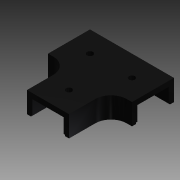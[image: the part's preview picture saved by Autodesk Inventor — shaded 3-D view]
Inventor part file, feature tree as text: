
AUTODESK INVENTOR PART (.ipt)
format: ipt  version: 2014 (Build 180170000, 170)  size: 173,056 bytes
history: native  units: in
note: dims shown in document units (in); Inventor stores cm internally (conversion verified against a paired STEP export)
features: extrude x6, sketch x6, other x3, split x1, fillet x1
ambient origin geometry x8: Origin, YZ Plane, XZ Plane, XY Plane, X Axis, Y Axis, Z Axis, Center Point
bodies: Solid1 (feature_tree)
feature tree (17):
  extrude  "Extrusion1"  Depth=1.0in
  extrude  "Extrusion2"  Depth=0.5in TaperAngle=0.0deg
  extrude  "Extrusion3"  Depth=0.75in
  extrude  "Extrusion4"  Depth=1.75in TaperAngle=0.0deg
  extrude  "Extrusion5"  Depth=0.75in
  split  "Split1"
  other  "Lip1"
  other  "Lip2"
  other  "Lip3"
  extrude  "Extrusion6"  Depth=0.375in
  fillet  "Fillet1"  Radius=1.0in
  sketch  "Sketch1"  dims[d0=1.0in d1=1.0in]
  sketch  "Sketch2"  dims[d2=2.0in d3=0.0in d4=0.5in d5=0.0in]
  sketch  "Sketch4"  dims[d6=0.5in d7=0.0in d8=0.75in]
  sketch  "Sketch5"  dims[d9=0.75in d10=1.75in d11=0.0in]
  sketch  "Sketch6"  dims[d12=0.75in d13=0.75in]
  sketch  "Sketch7"  dims[d14=1.75in d15=0.0in d16=0.03in d17=0.03in d18=0.0in d19=0.0in d20=0.0in d21=0.0in d22=0.03in d23=0.03in d24=0.0in d25=0.0in d26=0.0in d27=0.0in d28=0.03in d29=0.03in d30=0.0in d31=0.0in d32=0.0in d33=0.0in d34=0.141in d35=1.0in d36=0.0in d37=0.375in]
